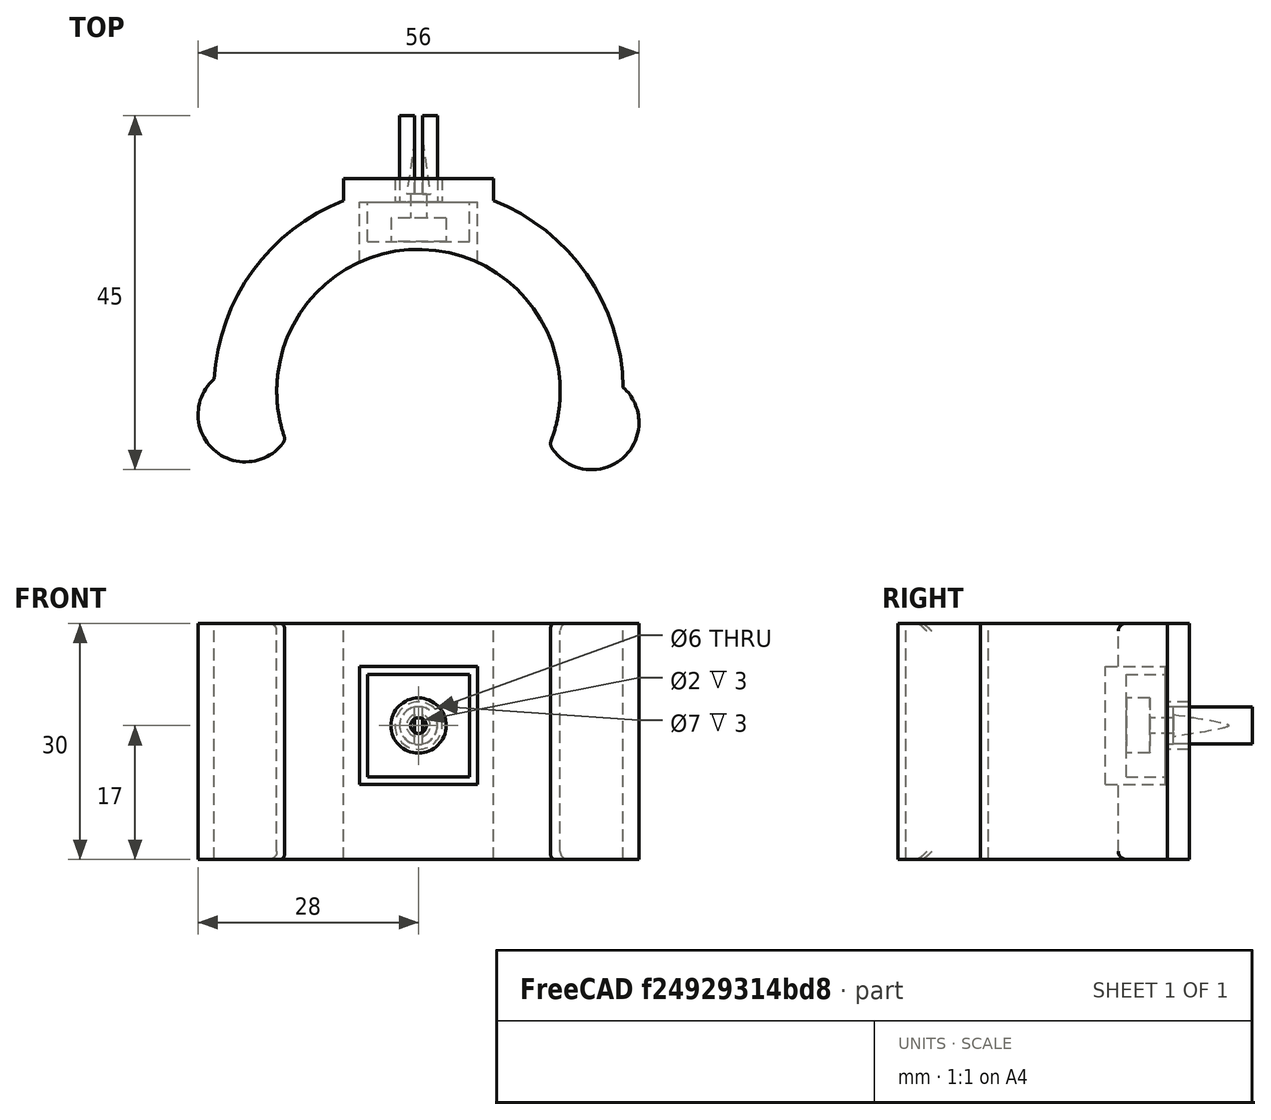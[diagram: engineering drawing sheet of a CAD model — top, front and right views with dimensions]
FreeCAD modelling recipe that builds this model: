
FCSTD DOCUMENT  (FreeCAD 0.16R5805 (Git))
Label: vacuum_cleaner_tube_holder
License: All rights reserved
LicenseURL: http://en.wikipedia.org/wiki/All_rights_reserved
objects: Part::Cylinder×8, Part::Box×4, Part::MultiFuse×4, Part::Cut×2, Part::Cone×1, Part::Fillet×1
note: 20 computed .brp shape members not serialized (recipe doc carries the construction recipe); baked Part::Feature solids carry a one-line shape summary decoded from their .brp

FEATURE [Part::Cylinder] Cylinder002  label="anchor pin"
  Angle = 360
  Height = 13
  Placement = pos=(18,72,6) rot=(1,0,0;1.5708rad)
  Radius = 2.4
FEATURE [Part::Box] Box  label="cut"
  Height = 10
  Length = 1
  Placement = pos=(17.5,62,1) rot=(0,0,1;0rad)
  Width = 10
FEATURE [Part::Cone] Cone  label="screw guide"
  Angle = 360
  Height = 7
  Placement = pos=(18,69,6) rot=(1,0,0;1.5708rad)
  Radius1 = 0.5
  Radius2 = 1.5
FEATURE [Part::Cylinder] Cylinder  label="hole"
  Angle = 360
  Height = 3
  Placement = pos=(18,62,6) rot=(1,0,0;1.5708rad)
  Radius = 1
FEATURE [Part::Cylinder] Cylinder005  label="screw head seat"
  Angle = 360
  Height = 3
  Placement = pos=(18,59,6) rot=(1,0,0;1.5708rad)
  Radius = 3.5
FEATURE [Part::MultiFuse] Fusion  label="hole and cut"
  Shapes = -> [Box,Cone,Cylinder,Cylinder005]
FEATURE [Part::Box] Box002  label="squared washer"
  Height = 13
  Length = 13
  Placement = pos=(11.5,56,-0.5) rot=(0,0,1;0rad)
  Width = 5
FEATURE [Part::MultiFuse] Fusion001  label="anchor"
  Shapes = -> [Cylinder002,Box002]
FEATURE [Part::Cut] Cut  label="Anchor with hole and cut"
  Base = -> Fusion001
  Tool = -> Fusion
FEATURE [Part::Cylinder] Cylinder006  label="vacuum cleaner tube template"
  Angle = 360
  Height = 32
  Placement = pos=(18,37,-12) rot=(0,0,1;0rad)
  Radius = 18
FEATURE [Part::Cylinder] Cylinder007  label="arms"
  Angle = 201
  Height = 30
  Placement = pos=(18,37,-11) rot=(0,0,-1;0.191986rad)
  Radius = 26
FEATURE [Part::Cylinder] Cylinder008  label="guide 1"
  Angle = 360
  Height = 30
  Placement = pos=(-4,34,-11) rot=(0,0,1;0rad)
  Radius = 6
FEATURE [Part::Cylinder] Cylinder009  label="guide 2"
  Angle = 360
  Height = 30
  Placement = pos=(40,33,-11) rot=(0,0,1;0rad)
  Radius = 6
FEATURE [Part::Box] Box003  label="anchor seat"
  Height = 15
  Length = 15
  Placement = pos=(10.5,53,-1.5) rot=(0,0,1;0rad)
  Width = 8
FEATURE [Part::Cylinder] Cylinder010  label="anchor pin seat"
  Angle = 360
  Height = 13
  Placement = pos=(18,72,6) rot=(1,0,0;1.5708rad)
  Radius = 3
FEATURE [Part::MultiFuse] Fusion003  label="holes"
  Shapes = -> [Box003,Cylinder006,Cylinder010]
FEATURE [Part::Box] Box004  label="stabilizer shim"
  Height = 30
  Length = 19
  Placement = pos=(8.5,61,-11) rot=(0,0,1;0rad)
  Width = 3
FEATURE [Part::MultiFuse] Fusion002  label="arms and guides"
  Shapes = -> [Cylinder008,Cylinder009,Cylinder007,Box004]
FEATURE [Part::Cut] Cut001  label="holder with holes"
  Base = -> Fusion002
  Tool = -> Fusion003
FEATURE [Part::Fillet] Fillet  label="holder with holes and fillets"
  Base = -> Cut001
  Edges = 6 edges r=1: [Edge41,Edge59,Edge60,Edge69,Edge71,Edge73]
